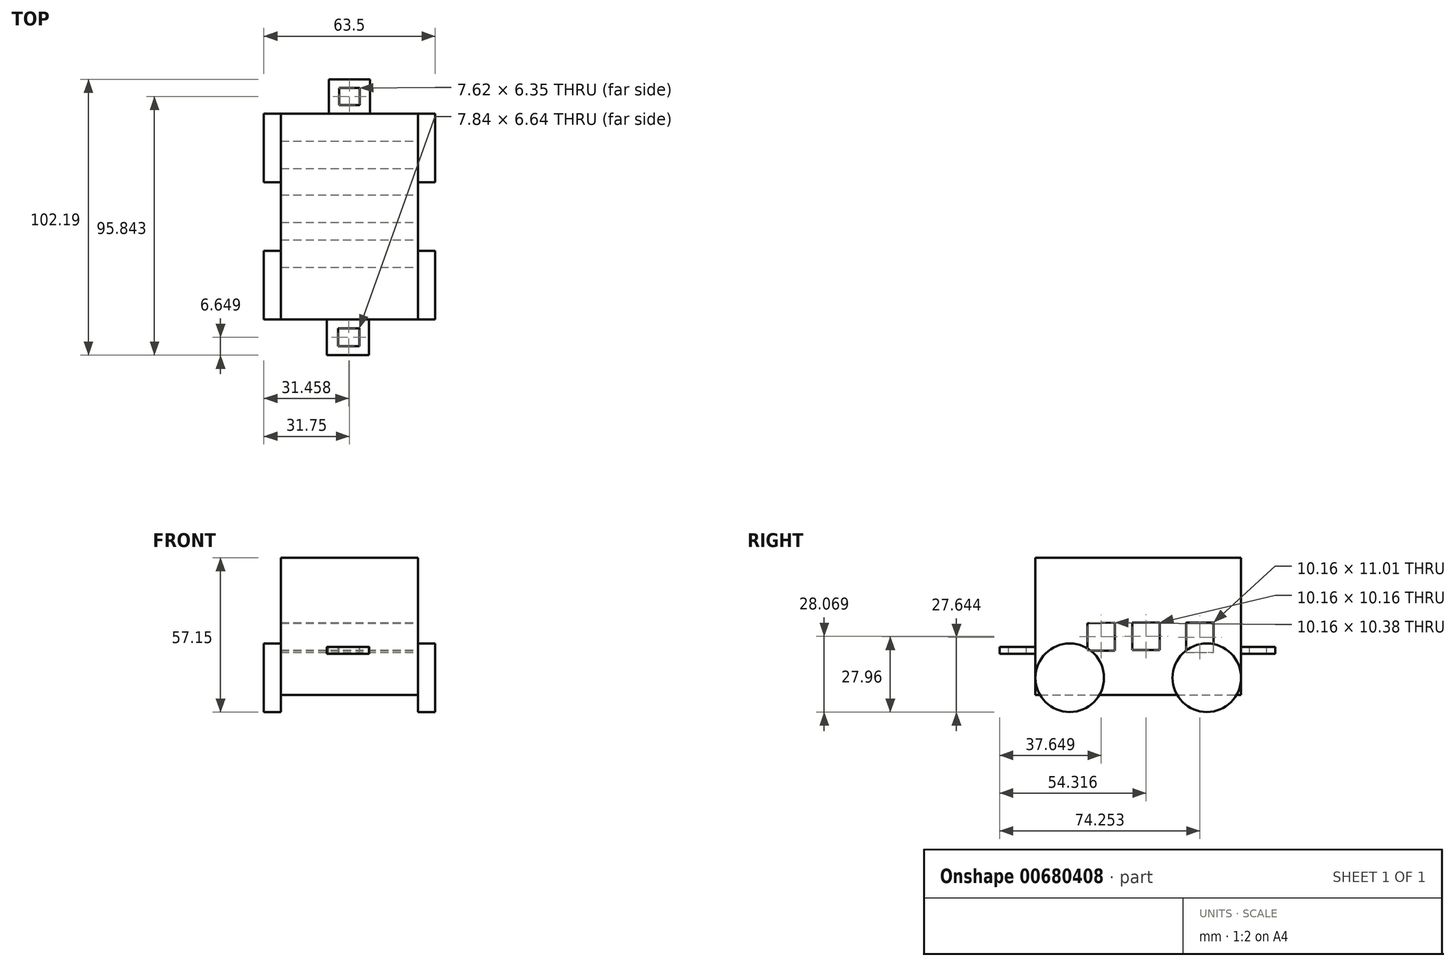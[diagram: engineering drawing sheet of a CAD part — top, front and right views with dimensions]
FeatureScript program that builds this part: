
annotation { "Feature Type Name" : "Feature", "Feature Type Description" : "" }
export const myFeature = defineFeature(function(context is Context, id is Id, definition is map)
    precondition{}
    {
        {
            var Q0;
            Q0=qCreatedBy(makeId("Right.planeOp"),FACE);
            var sketch = newSketch(context, id + "F0", { "sketchPlane" : qUnion([Q0])});
            skLineSegment(sketch, "E0", {"start": v(-19.28, 9.03) * mm, "end": v(56.92, 9.03) * mm});
            skLineSegment(sketch, "E1", {"start": v(56.92, 9.03) * mm, "end": v(56.92, -41.77) * mm});
            skLineSegment(sketch, "E2", {"start": v(-19.28, 9.03) * mm, "end": v(-19.28, -41.77) * mm});
            skLineSegment(sketch, "E3", {"start": v(-19.28, -41.77) * mm, "end": v(56.92, -41.77) * mm});
            skSolve(sketch);
        }
        {
            var Q0;
            Q0=qSketchRegion(id+"F0",true);
            extrude(context, id + "F1", {"entities" : qUnion([Q0]), "depth" : 50.8 * mm});
        }
        {
            var Q0;
            Q0=makeQuery(id+"F1.opExtrude","CAP_FACE",FACE,{"disambiguationData":[OSD([sQuery(id+"F0.wireOp",EDGE,"E0"),sQuery(id+"F0.wireOp",EDGE,"E1"),sQuery(id+"F0.wireOp",EDGE,"E2"),sQuery(id+"F0.wireOp",EDGE,"E3")])],"isStart":false});
            var sketch = newSketch(context, id + "F2", { "sketchPlane" : qUnion([Q0])});
            skLineSegment(sketch, "E4", {"start": v(0, -15.19) * mm, "end": v(0, -25.35) * mm});
            skLineSegment(sketch, "E5", {"start": v(0, -25.35) * mm, "end": v(10.16, -25.35) * mm});
            skLineSegment(sketch, "E6", {"start": v(10.16, -25.35) * mm, "end": v(10.16, -14.97) * mm});
            skLineSegment(sketch, "E7", {"start": v(0, -15.19) * mm, "end": v(10.16, -14.97) * mm});
            skLineSegment(sketch, "E8", {"start": v(16.67, -14.97) * mm, "end": v(26.83, -14.97) * mm});
            skLineSegment(sketch, "E9", {"start": v(26.83, -14.97) * mm, "end": v(26.83, -25.13) * mm});
            skLineSegment(sketch, "E10", {"start": v(26.83, -25.13) * mm, "end": v(16.67, -25.13) * mm});
            skLineSegment(sketch, "E11", {"start": v(16.67, -25.13) * mm, "end": v(16.67, -14.97) * mm});
            skLineSegment(sketch, "E12", {"start": v(-8.86, -15.19) * mm, "end": v(-8.86, -25.35) * mm});
            skLineSegment(sketch, "E13", {"start": v(-8.86, -25.35) * mm, "end": v(-19.02, -25.35) * mm});
            skLineSegment(sketch, "E14", {"start": v(-19.02, -25.35) * mm, "end": v(-19.02, -15.19) * mm});
            skLineSegment(sketch, "E15", {"start": v(-19.02, -15.19) * mm, "end": v(-8.86, -15.19) * mm});
            skPoint(sketch, "E16.start.orphan", {"position": v(47.54, -14.97) * mm});
            skLineSegment(sketch, "E17", {"start": v(36.6, -14.97) * mm, "end": v(36.6, -25.98) * mm});
            skLineSegment(sketch, "E18", {"start": v(36.6, -25.98) * mm, "end": v(46.76, -25.98) * mm});
            skLineSegment(sketch, "E19", {"start": v(46.76, -25.98) * mm, "end": v(46.76, -14.97) * mm});
            skLineSegment(sketch, "E20", {"start": v(46.76, -14.97) * mm, "end": v(36.6, -14.97) * mm});
            skSolve(sketch);
        }
        {
            var Q0;
            Q0=makeQuery(id+"F2.imprint","IMPRINT",FACE,{"disambiguationData":[TD([[makeQuery(id+"F2.imprint","IMPRINT",EDGE,{"derivedFrom":sQuery(id+"F2.wireOp",EDGE,"E4")}),1.0]])]});
            var Q1;
            Q1=makeQuery(id+"F2.imprint","IMPRINT",FACE,{"disambiguationData":[TD([[makeQuery(id+"F2.imprint","IMPRINT",EDGE,{"derivedFrom":sQuery(id+"F2.wireOp",EDGE,"E8")}),-1.0]])]});
            var Q2;
            Q2=makeQuery(id+"F2.imprint","IMPRINT",FACE,{"disambiguationData":[TD([[makeQuery(id+"F2.imprint","IMPRINT",EDGE,{"derivedFrom":sQuery(id+"F2.wireOp",EDGE,"E17")}),1.0]])]});
            extrude(context, id + "F3", {"entities" : qUnion([Q0, Q1, Q2]), "operationType" : NewBodyOperationType.REMOVE, "oppositeDirection" : true, "depth" : 50.8 * mm});
        }
        {
            var Q0;
            Q0=makeQuery(id+"F1.opExtrude","CAP_FACE",FACE,{"disambiguationData":[OSD([sQuery(id+"F0.wireOp",EDGE,"E0"),sQuery(id+"F0.wireOp",EDGE,"E1"),sQuery(id+"F0.wireOp",EDGE,"E2"),sQuery(id+"F0.wireOp",EDGE,"E3")])],"isStart":true});
            var sketch = newSketch(context, id + "F4", { "sketchPlane" : qUnion([Q0])});
            skCircle(sketch, "E21", {"center": v(-44.22, -35.42) * mm, "radius": 12.7 * mm});
            skCircle(sketch, "E22", {"center": v(6.58, -35.42) * mm, "radius": 12.7 * mm});
            skLineSegment(sketch, "E23", {"start": v(19.28, -16.37) * mm, "end": v(6.58, -35.42) * mm});
            skLineSegment(sketch, "E24", {"start": v(-44.22, -35.42) * mm, "end": v(-56.92, -20.05) * mm});
            skPoint(sketch, "E24.endSnap0", {"position": v(-16.67, -20.05) * mm});
            skLineSegment(sketch, "E25", {"start": v(6.58, -35.42) * mm, "end": v(6.58, 9.03) * mm});
            skLineSegment(sketch, "E26", {"start": v(-44.22, -35.42) * mm, "end": v(-44.22, 9.03) * mm});
            skSolve(sketch);
        }
        {
            var Q0;
            Q0=qSketchRegion(id+"F4",true);
            extrude(context, id + "F5", {"entities" : qUnion([Q0]), "depth" : 6.35 * mm});
        }
        {
            var Q0;
            Q0=makeQuery(id+"F1.opExtrude","CAP_FACE",FACE,{"disambiguationData":[OSD([sQuery(id+"F0.wireOp",EDGE,"E0"),sQuery(id+"F0.wireOp",EDGE,"E1"),sQuery(id+"F0.wireOp",EDGE,"E2"),sQuery(id+"F0.wireOp",EDGE,"E3")])],"isStart":false});
            var sketch = newSketch(context, id + "F6", { "sketchPlane" : qUnion([Q0])});
            skLineSegment(sketch, "E27", {"start": v(36.6, -25.26) * mm, "end": v(36.6, -25.98) * mm});
            skLineSegment(sketch, "E28", {"start": v(-6.58, -21.37) * mm, "end": v(-6.58, -22.72) * mm});
            skCircle(sketch, "E29", {"center": v(-6.58, -35.42) * mm, "radius": 12.7 * mm});
            skCircle(sketch, "E30", {"center": v(44.22, -35.42) * mm, "radius": 12.7 * mm});
            skLineSegment(sketch, "E31", {"start": v(-6.58, -35.42) * mm, "end": v(-19.28, -16.37) * mm});
            skLineSegment(sketch, "E32", {"start": v(44.22, -35.42) * mm, "end": v(56.92, -16.37) * mm});
            skLineSegment(sketch, "E33", {"start": v(-6.58, -35.42) * mm, "end": v(-6.58, 9.03) * mm});
            skLineSegment(sketch, "E34", {"start": v(44.22, -35.42) * mm, "end": v(44.22, 9.03) * mm});
            skSolve(sketch);
        }
        {
            var Q0;
            Q0=qSketchRegion(id+"F6",true);
            extrude(context, id + "F7", {"entities" : qUnion([Q0]), "depth" : 6.35 * mm});
        }
        {
            var Q0;
            Q0=makeQuery(id+"F1.opExtrude","SWEPT_FACE",FACE,{"disambiguationData":[OSD([sQuery(id+"F0.wireOp",EDGE,"E0")])]});
            var sketch = newSketch(context, id + "F8", { "sketchPlane" : qUnion([Q0])});
            skLineSegment(sketch, "E35", {"start": v(25.4, 56.92) * mm, "end": v(17.78, 56.92) * mm});
            skLineSegment(sketch, "E36", {"start": v(25.4, 56.92) * mm, "end": v(33.02, 56.92) * mm});
            skLineSegment(sketch, "E37", {"start": v(17.78, 56.92) * mm, "end": v(17.78, 69.62) * mm});
            skLineSegment(sketch, "E38", {"start": v(17.78, 69.62) * mm, "end": v(33.02, 69.62) * mm});
            skLineSegment(sketch, "E39", {"start": v(33.02, 69.62) * mm, "end": v(33.02, 56.92) * mm});
            skLineSegment(sketch, "E40", {"start": v(17.78, 63.27) * mm, "end": v(17.78, 69.62) * mm});
            skLineSegment(sketch, "E41", {"start": v(21.6, 66.45) * mm, "end": v(29.21, 66.45) * mm});
            skPoint(sketch, "E41.startSnap0", {"position": v(21.6, 56.92) * mm});
            skPoint(sketch, "E41.startSnap1", {"position": v(17.78, 66.45) * mm});
            skPoint(sketch, "E41.endSnap0", {"position": v(29.21, 56.92) * mm});
            skPoint(sketch, "E41.endSnap1", {"position": v(17.78, 66.45) * mm});
            skLineSegment(sketch, "E42", {"start": v(17.78, 63.27) * mm, "end": v(17.78, 56.92) * mm});
            skLineSegment(sketch, "E43", {"start": v(21.6, 60.1) * mm, "end": v(29.21, 60.1) * mm});
            skPoint(sketch, "E43.startSnap0", {"position": v(17.78, 60.1) * mm});
            skLineSegment(sketch, "E44", {"start": v(29.21, 60.1) * mm, "end": v(29.21, 66.45) * mm});
            skLineSegment(sketch, "E45", {"start": v(21.6, 66.45) * mm, "end": v(21.6, 60.1) * mm});
            skLineSegment(sketch, "E46", {"start": v(25.4, -19.28) * mm, "end": v(32.66, -19.28) * mm});
            skLineSegment(sketch, "E47", {"start": v(32.66, -19.28) * mm, "end": v(32.66, -32.57) * mm});
            skLineSegment(sketch, "E48", {"start": v(32.66, -32.57) * mm, "end": v(16.97, -32.57) * mm});
            skLineSegment(sketch, "E49", {"start": v(16.97, -32.57) * mm, "end": v(16.97, -19.28) * mm});
            skLineSegment(sketch, "E50", {"start": v(16.97, -19.28) * mm, "end": v(25.4, -19.28) * mm});
            skLineSegment(sketch, "E51", {"start": v(32.66, -25.92) * mm, "end": v(32.66, -19.28) * mm});
            skLineSegment(sketch, "E52", {"start": v(32.66, -25.92) * mm, "end": v(32.66, -32.57) * mm});
            skLineSegment(sketch, "E53", {"start": v(29.03, -29.24) * mm, "end": v(21.19, -29.24) * mm});
            skPoint(sketch, "E53.startSnap0", {"position": v(29.03, -19.28) * mm});
            skPoint(sketch, "E53.startSnap1", {"position": v(32.66, -29.24) * mm});
            skPoint(sketch, "E53.endSnap0", {"position": v(21.19, -19.28) * mm});
            skLineSegment(sketch, "E54", {"start": v(21.19, -29.24) * mm, "end": v(21.19, -22.6) * mm});
            skPoint(sketch, "E54.endSnap0", {"position": v(32.66, -22.6) * mm});
            skLineSegment(sketch, "E55", {"start": v(21.19, -22.6) * mm, "end": v(29.03, -22.6) * mm});
            skLineSegment(sketch, "E56", {"start": v(29.03, -22.6) * mm, "end": v(29.03, -29.24) * mm});
            skSolve(sketch);
        }
        {
            var Q0;
            Q0=qSketchRegion(id+"F8",true);
            extrude(context, id + "F9", {"entities" : qUnion([Q0]), "operationType" : NewBodyOperationType.ADD, "oppositeDirection" : true, "depth" : 35.56 * mm});
        }
        {
            var Q0;
            Q0=qSketchRegion(id+"F8",true);
            extrude(context, id + "F10", {"entities" : qUnion([Q0]), "operationType" : NewBodyOperationType.REMOVE, "oppositeDirection" : true, "depth" : 33.02 * mm});
        }
    });
